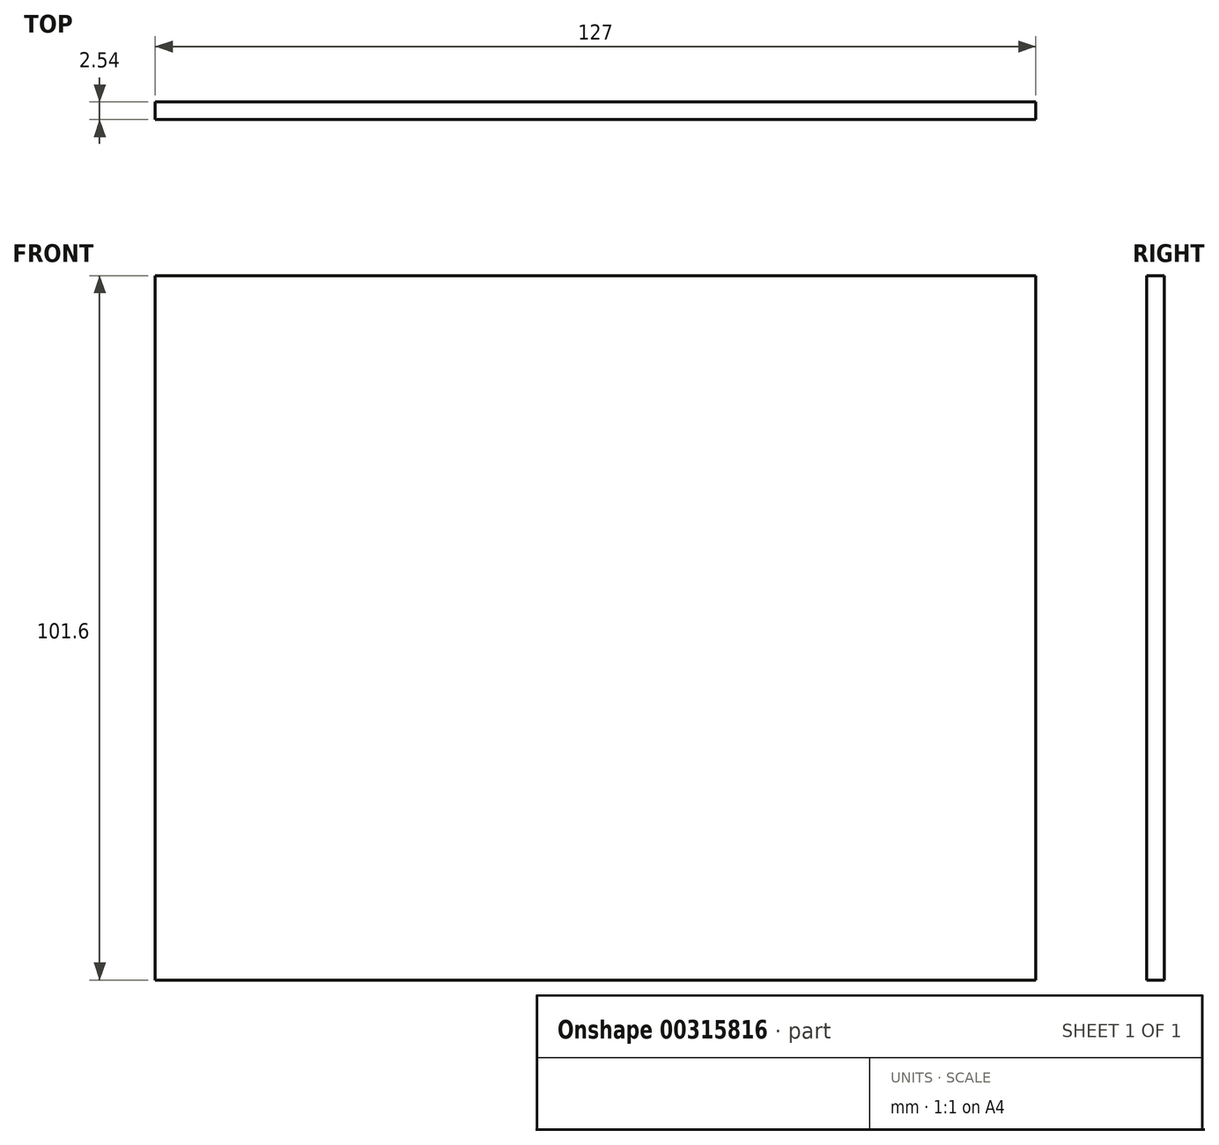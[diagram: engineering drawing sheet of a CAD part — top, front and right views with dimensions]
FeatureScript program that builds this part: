
annotation { "Feature Type Name" : "Feature", "Feature Type Description" : "" }
export const myFeature = defineFeature(function(context is Context, id is Id, definition is map)
    precondition{}
    {
        {
            var Q0;
            Q0=qCreatedBy(makeId("Front.planeOp"),FACE);
            var sketch = newSketch(context, id + "F0", { "sketchPlane" : qUnion([Q0])});
            skLineSegment(sketch, "E0.bottom", {"start": v(-63.5, 50.8) * mm, "end": v(63.5, 50.8) * mm});
            skLineSegment(sketch, "E0.top", {"start": v(-63.5, -50.8) * mm, "end": v(63.5, -50.8) * mm});
            skLineSegment(sketch, "E0.left", {"start": v(-63.5, 50.8) * mm, "end": v(-63.5, -50.8) * mm});
            skLineSegment(sketch, "E0.right", {"start": v(63.5, 50.8) * mm, "end": v(63.5, -50.8) * mm});
            skSolve(sketch);
        }
        {
            var Q0;
            Q0 = qSketchRegion(id + "F0", true);
            var Q1;
            Q1=makeQuery(id+"F0.imprint","IMPRINT",FACE,{"disambiguationData":[TD([[makeQuery(id+"F0.imprint","IMPRINT",EDGE,{"derivedFrom":sQuery(id+"F0.wireOp",EDGE,"E0.bottom")}),-1.0]])]});
            extrude(context, id + "F1", {"entities" : qUnion([Q0, Q1]), "depth" : 2.54 * mm});
        }
    });
